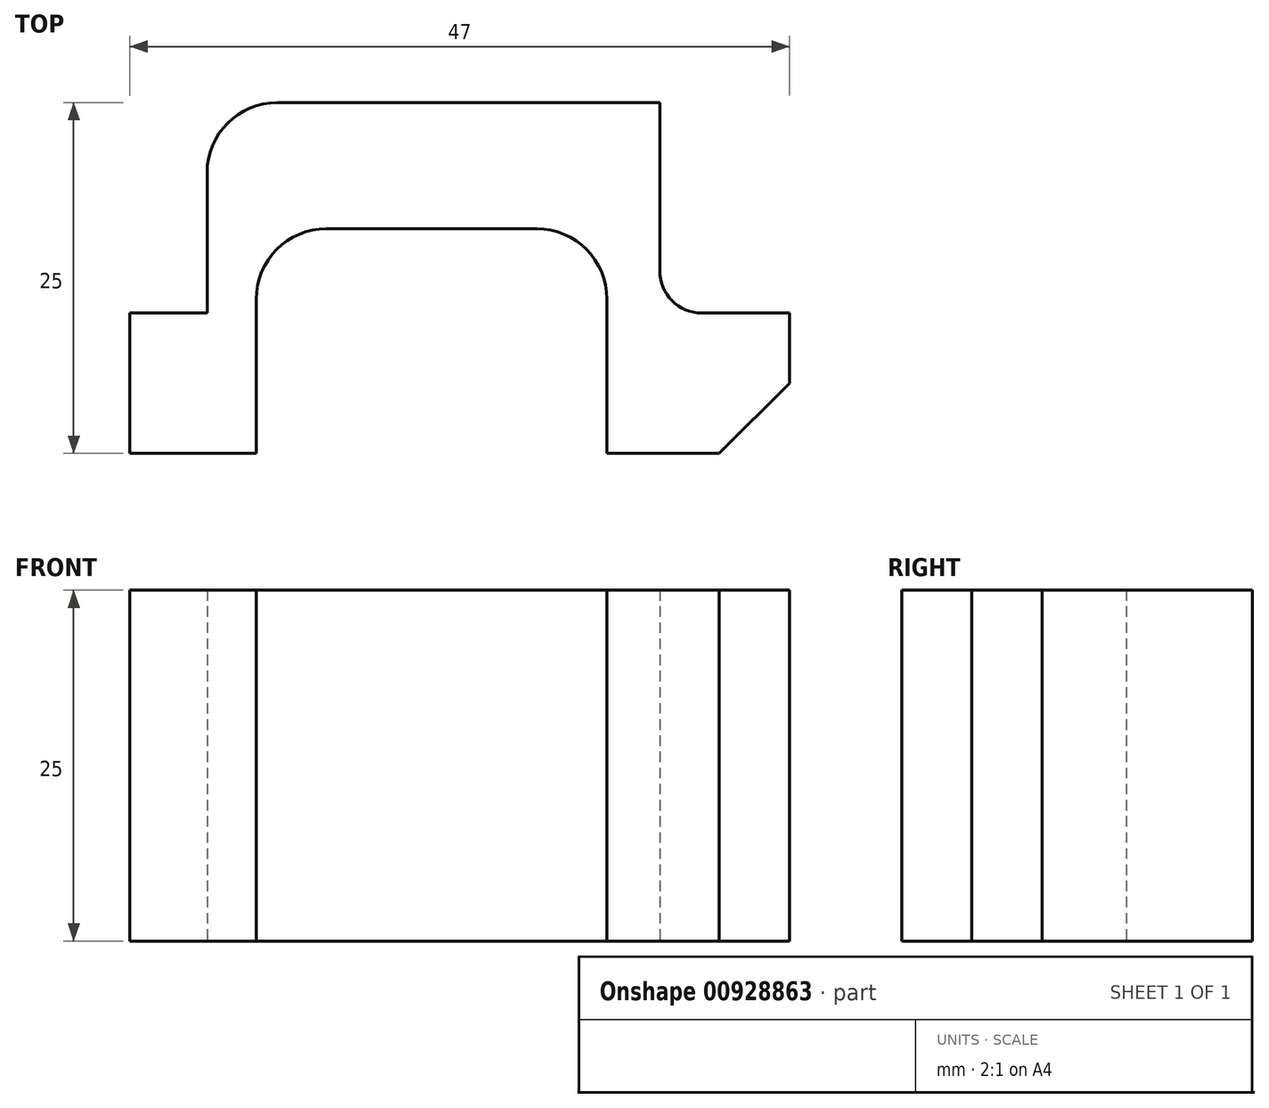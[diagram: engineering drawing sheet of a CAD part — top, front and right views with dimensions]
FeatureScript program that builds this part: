
annotation { "Feature Type Name" : "Feature", "Feature Type Description" : "" }
export const myFeature = defineFeature(function(context is Context, id is Id, definition is map)
    precondition{}
    {
        {
            var Q0;
            Q0=qCreatedBy(makeId("Top.planeOp"),FACE);
            var sketch = newSketch(context, id + "F0", { "sketchPlane" : qUnion([Q0])});
            skLineSegment(sketch, "E0.bottom", {"start": v(-9, 15) * mm, "end": v(38, 15) * mm});
            skLineSegment(sketch, "E0.top", {"start": v(-9, -10) * mm, "end": v(38, -10) * mm});
            skLineSegment(sketch, "E0.left", {"start": v(-9, 15) * mm, "end": v(-9, -10) * mm});
            skLineSegment(sketch, "E0.right", {"start": v(38, 15) * mm, "end": v(38, -10) * mm});
            skLineSegment(sketch, "E1.bottom", {"start": v(0, 6) * mm, "end": v(25, 6) * mm});
            skLineSegment(sketch, "E1.top", {"start": v(0, -10) * mm, "end": v(25, -10) * mm});
            skLineSegment(sketch, "E1.left", {"start": v(0, 6) * mm, "end": v(0, 0) * mm});
            skLineSegment(sketch, "E1.right", {"start": v(25, 6) * mm, "end": v(25, 0) * mm});
            skLineSegment(sketch, "E2.bottom", {"start": v(28.76, 0) * mm, "end": v(38, 0) * mm});
            skLineSegment(sketch, "E2.top", {"start": v(25, 15) * mm, "end": v(38, 15) * mm});
            skLineSegment(sketch, "E2.left", {"start": v(25, 0) * mm, "end": v(25, 6) * mm});
            skLineSegment(sketch, "E2.right", {"start": v(38, 0) * mm, "end": v(38, 15) * mm});
            skLineSegment(sketch, "E3.bottom", {"start": v(-9, 0) * mm, "end": v(-3.5, 0) * mm});
            skLineSegment(sketch, "E3.top", {"start": v(-9, -10) * mm, "end": v(0, -10) * mm});
            skLineSegment(sketch, "E3.left", {"start": v(-9, 0) * mm, "end": v(-9, -10) * mm});
            skLineSegment(sketch, "E4.bottom", {"start": v(25, 15) * mm, "end": v(28.76, 15) * mm});
            skLineSegment(sketch, "E4.right", {"start": v(28.76, 15) * mm, "end": v(28.76, 0) * mm});
            skLineSegment(sketch, "E5.right", {"start": v(38, 10) * mm, "end": v(38, 15) * mm});
            skLineSegment(sketch, "E6", {"start": v(28.76, 15) * mm, "end": v(28.76, 15) * mm});
            skLineSegment(sketch, "E7.top", {"start": v(0, 15) * mm, "end": v(-3.5, 15) * mm});
            skLineSegment(sketch, "E7.left", {"start": v(0, 0) * mm, "end": v(0, 6) * mm});
            skLineSegment(sketch, "E7.right", {"start": v(-3.5, 0) * mm, "end": v(-3.5, 15) * mm});
            skLineSegment(sketch, "E8", {"start": v(0, 0) * mm, "end": v(0, -10) * mm});
            skLineSegment(sketch, "E9", {"start": v(25, 0) * mm, "end": v(25, -10) * mm});
            skSolve(sketch);
        }
        {
            var Q0;
            Q0=makeQuery(id+"F0.imprint","IMPRINT",FACE,{"disambiguationData":[TD([[makeQuery(id+"F0.imprint","IMPRINT",EDGE,{"derivedFrom":sQuery(id+"F0.wireOp",EDGE,"E0.top")}),1.0]])]});
            extrude(context, id + "F1", {"entities" : qUnion([Q0]), "depth" : 25 * mm, "offsetDistance" : 25 * mm});
        }
        {
            var Q0;
            Q0=makeQuery(id+"F1.opExtrude","SWEPT_EDGE",EDGE,{"disambiguationData":[OSD([sQuery(id+"F0.wireOp",EDGE,"E0.bottom"),sQuery(id+"F0.wireOp",EDGE,"E7.top"),sQuery(id+"F0.wireOp",EDGE,"E7.right")])]});
            var Q1;
            Q1=makeQuery(id+"F1.opExtrude","SWEPT_EDGE",EDGE,{"disambiguationData":[OSD([sQuery(id+"F0.wireOp",EDGE,"E2.top"),sQuery(id+"F0.wireOp",EDGE,"E6")])]});
            var Q2;
            Q2=makeQuery(id+"F1.opExtrude","SWEPT_EDGE",EDGE,{"disambiguationData":[OSD([sQuery(id+"F0.wireOp",EDGE,"E1.bottom"),sQuery(id+"F0.wireOp",EDGE,"E7.left")])]});
            var Q3;
            Q3=makeQuery(id+"F1.opExtrude","SWEPT_EDGE",EDGE,{"disambiguationData":[OSD([sQuery(id+"F0.wireOp",EDGE,"E1.bottom"),sQuery(id+"F0.wireOp",EDGE,"E1.right")])]});
            fillet(context, id + "F2", {"entities" : qUnion([Q0, Q1, Q2, Q3]), "radius" : 5 * mm, "tangentPropagation" : true, "allowEdgeOverflow" : false});
        }
        {
            var Q0;
            Q0=makeQuery(id+"F1.opExtrude","SWEPT_EDGE",EDGE,{"disambiguationData":[OSD([sQuery(id+"F0.wireOp",EDGE,"E2.bottom"),sQuery(id+"F0.wireOp",EDGE,"E4.right")])]});
            fillet(context, id + "F3", {"entities" : qUnion([Q0]), "radius" : 3 * mm, "tangentPropagation" : true, "allowEdgeOverflow" : false});
        }
        {
            var Q0;
            Q0=makeQuery(id+"F1.opExtrude","SWEPT_EDGE",EDGE,{"disambiguationData":[OSD([sQuery(id+"F0.wireOp",EDGE,"E0.top"),sQuery(id+"F0.wireOp",EDGE,"E0.right")])]});
            chamfer(context, id + "F4", {"entities" : qUnion([Q0]), "width" : 5 * mm, "tangentPropagation" : true});
        }
    });
